# Revit family: OWEZVL
name_source: partatom
category: Mechanical Equipment
units: mm (PartAtom-declared; Revit-internal decimal feet)

## family parameters
Always vertical = Yes
Cut with Voids When Loaded = No
OmniClass Number = 23.40.40.11.17
OmniClass Title = Refrigerated Cases
Part Type = Normal
Room Calculation Point = No
Round Connector Dimension = Use Radius
Shared = No
Work Plane-Based = Yes

## types (45) — shared parameters
Case Type/Application = Medium Temp
Certifications = NSF 7, UL471, CSA
DATE = 12-14-2015
DESIGNERS NAME = SHIDDRAMESH
Default Elevation = 48"
Description = OWIZV-Gaint Eagel
EQUIPMENT DESCRIPTION = OWIZV-Gaint Eagel
EQUIPMENT MARK = OWIZV- 7BF
GLASS = Glass
Height = 38 1/8"
How Many Defrosts Per Day = 1
Island Discharge Air Velocity (FPM) = 180 FPM
Island Electric Fail-Safe = 60 (Min)
Island Electric Run-Off Time (Min) = 0 (Min)
Island Electric Termination Temp (F°) = 49 °F
Island High Efficiency Fans Amps = 0 A
Island Hot Gas Fail-Safe (Min) = 10 (Min)
Island Hot Gas Run-Off Time (Min) = 0 (Min)
Island Hot Gas Termination Temp (F°) = 60 °F
Island Tank/Drain Heater Amps = 0 A
Island Tank/Drain Heater Watts = 30 W
Island Timed-Off Fail-Safe (Min) = 35 (Min)
Island Timed-Off Termination Temp (°F) = 42 °F
Item Description = OWIZV-Gaint Eagel
Legend Number = OWIZV- 7BF
Manufacturer = HILL PHOENIX
Model = OWIZV- 7BF
PAINTED METAL UPPER SHELF = PAINTED SHELVES
REF PLANE LEFT RIGHT = 41 7/16"
REFRIGERATION PIPING = COPPER PIPE
SHELF 10" = No
SHELF 16" = No
STAINLESS STEEL = GALVANIZED STEEL
SUPERSTRUCTURE 48" = No
SUPERSTRUCTURE 52" = No
SUPERSTRUCTURE 60" = No
URL = http://www.hillphoenix.com
Width = 82 7/8"

## per-type parameters (varying)
| type | CENTER LINE | High Power (Cornice) Amps | High Power (Cornice) Watts | Island  Case Length | Island 208V Defrost Heaters Amps | Island 208V Defrost Heaters Watts | Island 240 Defrost Heaters Amps | Island 240 Defrost Heaters Watts | Island Anti-Condensate Heaters Amps | Island Anti-Condensate Heaters Watts | Island Application | Island BTUH Conventional | Island BTUH Parallel | Island Discharge Air(°F) | Island Evaporator (°F) | Island Fans Per Case | Island High Efficiency Fans Watts | Island Superheat @ Bulb Set Point (°F) | Length | Light Length | Lights Per Row | Standard Power Amps | Standard Power Watts |
| 10' - Ice Cream - Solid Front | 60" | 1 A | 103 W | 120" | 14 A | 3000 A | 17 A | 3994 W | 2 A | 288 W | Ice Cream | 719 | 692 | -17 °F | -22 °F | 6 | 24 W | 3-5 °F | 120" | 2-3 , 1-4' | 6 | 0 A | 57 W |
| 08' - Medium Temp - Solid Front | 48" | 1 A | 86 W | 96" | 12 A | 2400 A | 13 A | 3198 W | 2 A | 220 W | Medium Temp | 458 | 450 | 27 °F | 17 °F | 4 | 16 W | 6-8 °F | 96" | 4-4' | 4 | 0 A | 48 W |
| 06' - Medium Temp - Solid Front | 36" | 1 A | 60 W | 72" | 9 A | 1800 A | 10 A | 2400 W | 1 A | 160 W | Medium Temp | 458 | 450 | 27 °F | 17 °F | 4 | 16 W | 6-8 °F | 72" | 2-3' | 4 | 0 A | 33 W |
| 12' - Medium Temp - Solid Front | 72" | 1 A | 129 W | 144" | 17 A | 3600 A | 20 A | 4795 W | 3 A | 344 W | Medium Temp | 458 | 450 | 27 °F | 17 °F | 6 | 24 W | 6-8 °F | 144" | 3-4' | 6 | 1 A | 71 W |
| 04' - Medium Temp - Solid Front | 24" | 0 A | 43 W | 48" | 8 A | 1600 A | 9 A | 2130 W | 1 A | 124 W | Medium Temp | 458 | 450 | 27 °F | 17 °F | 2 | 8 W | 6-8 °F | 48" | 2-4' | 2 | 0 A | 24 W |
| 04' - Frozen Food - Solid Front | 24" | 0 A | 43 W | 48" | 8 A | 1600 A | 9 A | 2130 W | 1 A | 124 W | Frozen Food | 610 | 587 | 16 °F | 12 °F | 2 | 8 W | 3-5 °F | 48" | 2-4' | 2 | 0 A | 24 W |
| 04' - Ice Cream - Solid Front | 24" | 0 A | 43 W | 48" | 8 A | 1600 A | 9 A | 2130 W | 1 A | 124 W | Ice Cream | 719 | 692 | -17 °F | -22 °F | 2 | 8 W | 3-5 °F | 48" | 2-4' | 2 | 0 A | 24 W |
| 04' - Frozen Food - Glass  Front | 24" | 0 A | 43 W | 48" | 8 A | 1600 A | 9 A | 2130 W | 1 A | 162 W | Frozen Food | 610 | 587 | 16 °F | 12 °F | 2 | 8 W | 3-5 °F | 48" | 2-4' | 2 | 0 A | 24 W |
| 04' - Frozen Food - Glass Wrap  Front | 24" | 0 A | 43 W | 48" | 8 A | 1600 A | 9 A | 2130 W | 1 A | 68 W | Frozen Food | 610 | 587 | 16 °F | 12 °F | 2 | 8 W | 3-5 °F | 48" | 2-4' | 2 | 0 A | 24 W |
| 04' - Medium Temp - Glass Wrap Front | 24" | 0 A | 43 W | 48" | 8 A | 1600 A | 9 A | 2130 W | 1 A | 68 W | Medium Temp | 458 | 450 | 27 °F | 17 °F | 2 | 8 W | 6-8 °F | 48" | 2-4' | 2 | 0 A | 24 W |
| 04' - Medium Temp - Glass Front | 24" | 0 A | 43 W | 48" | 8 A | 1600 A | 9 A | 2130 W | 1 A | 162 W | Medium Temp | 458 | 450 | 27 °F | 17 °F | 2 | 8 W | 6-8 °F | 48" | 2-4' | 2 | 0 A | 24 W |
| 04' - Ice Cream - Glass Wrap Front | 24" | 0 A | 43 W | 48" | 8 A | 1600 A | 9 A | 2130 W | 1 A | 68 W | Ice Cream | 719 | 692 | -17 °F | -22 °F | 2 | 8 W | 3-5 °F | 48" | 2-4' | 2 | 0 A | 24 W |
| 04' - Ice Cream - Glass  Front | 24" | 0 A | 43 W | 48" | 8 A | 1600 A | 9 A | 2130 W | 1 A | 162 W | Ice Cream | 719 | 692 | -17 °F | -22 °F | 2 | 8 W | 3-5 °F | 48" | 2-4' | 2 | 0 A | 24 W |
| 06' - Frozen Food - Solid Front | 36" | 1 A | 60 W | 72" | 9 A | 1800 A | 10 A | 2400 W | 1 A | 160 W | Frozen Food | 610 | 587 | -6 °F | -12 °F | 4 | 16 W | 3-5 °F | 72" | 2-3' | 4 | 0 A | 33 W |
| 06' - Ice Cream - Solid Front | 36" | 1 A | 60 W | 72" | 9 A | 1800 A | 10 A | 2400 W | 1 A | 160 W | Ice Cream | 719 | 692 | -17 °F | -22 °F | 4 | 16 W | 3-5 °F | 72" | 2-3' | 4 | 0 A | 33 W |
| 06' - Ice Cream - Glass Wrap Front | 36" | 1 A | 60 W | 72" | 9 A | 1800 A | 10 A | 2400 W | 1 A | 68 W | Ice Cream | 719 | 692 | -17 °F | -22 °F | 4 | 16 W | 3-5 °F | 72" | 2-3' | 4 | 0 A | 33 W |
| 06' - Ice Cream - Glass  Front | 36" | 1 A | 60 W | 72" | 9 A | 1800 A | 10 A | 2 W | 222 A | 68 W | Ice Cream | 719 | 692 | -17 °F | -22 °F | 4 | 16 W | 3-5 °F | 72" | 2-3' | 4 | 0 A | 33 W |
| 06' - Frozen Food - Glass Wrap  Front | 36" | 1 A | 60 W | 72" | 9 A | 1800 A | 10 A | 2400 W | 1 A | 68 W | Frozen Food | 610 | 587 | -6 °F | -12 °F | 4 | 16 W | 3-5 °F | 72" | 2-3' | 4 | 0 A | 33 W |
| 06' - Frozen Food - Glass Front | 36" | 1 A | 60 W | 72" | 9 A | 1800 A | 10 A | 2400 W | 2 A | 222 W | Frozen Food | 610 | 587 | -6 °F | -12 °F | 4 | 16 W | 3-5 °F | 72" | 2-3' | 4 | 0 A | 33 W |
| 06' - Medium Temp - Glass Wrap Front | 36" | 1 A | 60 W | 72" | 9 A | 1800 A | 10 A | 2400 W | 1 A | 68 W | Medium Temp | 458 | 450 | 27 °F | 17 °F | 4 | 16 W | 6-8 °F | 72" | 2-3' | 4 | 0 A | 33 W |
| 06' - Medium Temp - Glass  Front | 36" | 1 A | 60 W | 72" | 9 A | 1800 A | 10 A | 2400 W | 2 A | 222 W | Medium Temp | 458 | 450 | 27 °F | 17 °F | 4 | 16 W | 6-8 °F | 72" | 2-3' | 4 | 0 A | 33 W |
| 08' - Ice Cream - Solid Front | 48" | 1 A | 86 W | 96" | 12 A | 2400 A | 13 A | 3198 W | 2 A | 220 W | Ice Cream | 719 | 692 | -17 °F | -22 °F | 4 | 16 W | 3-5 °F | 96" | 4-4' | 4 | 0 A | 48 W |
| 08' - Frozen Food - Solid Front | 48" | 1 A | 86 W | 96" | 12 A | 2400 A | 13 A | 3198 W | 2 A | 220 W | Frozen Food | 610 | 587 | -6 °F | -12 °F | 4 | 16 W | 3-5 °F | 96" | 4-4' | 4 | 0 A | 48 W |
| 08' - Frozen Food - Glass Wrap Front | 48" | 1 A | 86 W | 96" | 12 A | 2400 A | 13 A | 3198 W | 2 A | 290 W | Frozen Food | 610 | 587 | -6 °F | -12 °F | 4 | 16 W | 3-5 °F | 96" | 4-4' | 4 | 0 A | 48 W |
| 08' - Frozen Food - Glass  Front | 48" | 1 A | 86 W | 96" | 12 A | 2400 A | 13 A | 3198 W | 1 A | 68 W | Frozen Food | 610 | 587 | -6 °F | -12 °F | 4 | 16 W | 3-5 °F | 96" | 4-4' | 4 | 0 A | 48 W |
| 08' - Ice Cream - Glass Wrap Front | 48" | 1 A | 86 W | 96" | 12 A | 2400 A | 13 A | 3198 W | 2 A | 290 W | Ice Cream | 719 | 692 | -17 °F | -22 °F | 4 | 16 W | 3-5 °F | 96" | 4-4' | 4 | 0 A | 48 W |
| 08' - Ice Cream - Glass  Front | 48" | 1 A | 86 W | 96" | 12 A | 2400 A | 13 A | 3198 W | 1 A | 68 W | Ice Cream | 719 | 692 | -17 °F | -22 °F | 4 | 16 W | 3-5 °F | 96" | 4-4' | 4 | 0 A | 48 W |
| 08' - Medium Temp - Glass Wrap Front | 48" | 1 A | 86 W | 96" | 12 A | 2400 A | 13 A | 3198 W | 2 A | 290 W | Medium Temp | 458 | 450 | 27 °F | 17 °F | 4 | 16 W | 6-8 °F | 96" | 4-4' | 4 | 0 A | 48 W |
| 08' - Medium Temp - Glass  Front | 48" | 1 A | 86 W | 96" | 12 A | 2400 A | 13 A | 3198 W | 1 A | 68 W | Medium Temp | 458 | 450 | 27 °F | 17 °F | 4 | 16 W | 6-8 °F | 96" | 4-4' | 4 | 0 A | 48 W |
| 10' - Frozen Food - Solid Front | 60" | 1 A | 103 W | 120" | 14 A | 3000 A | 17 A | 3994 W | 2 A | 288 W | Frozen Food | 610 | 587 | -6 °F | -12 °F | 6 | 24 W | 3-5 °F | 120" | 2-3 , 1-4' | 6 | 0 A | 57 W |
| 10' - Frozen Food - Glass Wrap Front | 60" | 1 A | 103 W | 120" | 14 A | 3000 A | 17 A | 3994 W | 1 A | 68 W | Frozen Food | 610 | 587 | -6 °F | -12 °F | 6 | 24 W | 3-5 °F | 120" | 2-3 , 1-4' | 6 | 0 A | 57 W |
| 10' - Frozen Food - Glass  Front | 60" | 1 A | 103 W | 120" | 14 A | 3000 A | 17 A | 3994 W | 3 A | 368 W | Frozen Food | 610 | 587 | -6 °F | -12 °F | 6 | 24 W | 3-5 °F | 120" | 2-3 , 1-4' | 6 | 0 A | 57 W |
| 10' - Medium Temp - Solid Front | 60" | 1 A | 103 W | 120" | 14 A | 3000 A | 17 A | 3994 W | 2 A | 288 W | Medium Temp | 458 | 450 | 27 °F | 17 °F | 6 | 24 W | 6-8 °F | 120" | 2-3 , 1-4' | 6 | 0 A | 57 W |
| 10' - Medium Temp - Glass Wrap Front | 60" | 1 A | 103 W | 120" | 14 A | 3000 A | 17 A | 3994 W | 1 A | 68 W | Medium Temp | 458 | 450 | 27 °F | 17 °F | 6 | 24 W | 6-8 °F | 120" | 2-3 , 1-4' | 6 | 0 A | 57 W |
| 10' - Medium Temp - Glass  Front | 60" | 1 A | 103 W | 120" | 14 A | 3000 A | 17 A | 3994 W | 3 A | 368 W | Medium Temp | 458 | 450 | 27 °F | 17 °F | 6 | 24 W | 6-8 °F | 120" | 2-3 , 1-4' | 6 | 0 A | 57 W |
| 10' - Ice Cream - Glass Wrap Front | 60" | 1 A | 103 W | 120" | 14 A | 3000 A | 17 A | 3994 W | 1 A | 68 W | Ice Cream | 719 | 692 | -17 °F | -22 °F | 6 | 24 W | 3-5 °F | 120" | 2-3 , 1-4' | 6 | 0 A | 57 W |
| 10' - Ice Cream - Glass  Front | 60" | 1 A | 103 W | 120" | 14 A | 3000 A | 17 A | 3994 W | 3 A | 368 W | Ice Cream | 719 | 692 | -17 °F | -22 °F | 6 | 24 W | 3-5 °F | 120" | 2-3 , 1-4' | 6 | 0 A | 57 W |
| 12' - Ice Cream - Solid Front | 72" | 1 A | 129 W | 144" | 17 A | 3600 A | 20 A | 4795 W | 3 A | 344 W | Ice Cream | 719 | 692 | -17 °F | -22 °F | 6 | 24 W | 3-5 °F | 144" | 3-4' | 6 | 1 A | 71 W |
| 12' - Ice Cream - Glass Wrap Front | 72" | 1 A | 129 W | 144" | 17 A | 3600 A | 20 A | 4795 W | 1 A | 68 W | Ice Cream | 719 | 692 | -17 °F | -22 °F | 6 | 24 W | 3-5 °F | 144" | 3-4' | 6 | 1 A | 71 W |
| 12' - Ice Cream - Glass  Front | 72" | 1 A | 129 W | 144" | 17 A | 3600 A | 20 A | 4795 W | 4 A | 454 W | Ice Cream | 719 | 692 | -17 °F | -22 °F | 6 | 24 W | 3-5 °F | 144" | 3-4' | 6 | 1 A | 71 W |
| 12' - Medium Temp - Glass Wrap Front | 72" | 1 A | 129 W | 144" | 17 A | 3600 A | 20 A | 4795 W | 6 A | 68 W | Medium Temp | 458 | 450 | 27 °F | 17 °F | 6 | 24 W | 6-8 °F | 144" | 3-4' | 6 | 1 A | 71 W |
| 12' - Medium Temp - Glass  Front | 72" | 1 A | 129 W | 144" | 17 A | 3600 A | 20 A | 4795 W | 4 A | 454 W | Medium Temp | 458 | 450 | 27 °F | 17 °F | 6 | 24 W | 6-8 °F | 144" | 3-4' | 6 | 1 A | 71 W |
| 12' - Frozen Food - Solid Front | 72" | 1 A | 129 W | 144" | 17 A | 3600 A | 20 A | 4795 W | 3 A | 344 W | Frozen Food | 610 | 587 | -6 °F | -12 °F | 6 | 24 W | 3-5 °F | 144" | 3-4' | 6 | 1 A | 71 W |
| 12' - Frozen Food - Glass Wrap  Front | 72" | 1 A | 129 W | 144" | 17 A | 3600 A | 20 A | 4795 W | 1 A | 68 W | Frozen Food | 610 | 587 | -6 °F | -12 °F | 6 | 24 W | 3-5 °F | 144" | 3-4' | 6 | 1 A | 71 W |
| 12' - Frozen Food - Glass Front | 72" | 1 A | 129 W | 144" | 17 A | 3600 A | 20 A | 4795 W | 4 A | 454 W | Frozen Food | 610 | 587 | -6 °F | -12 °F | 6 | 24 W | 3-5 °F | 144" | 3-4' | 6 | 1 A | 71 W |

## geometry (parser evidence)
native form markers: Blend x8, Sweep x11
no freeform markers — native parametric forms only
